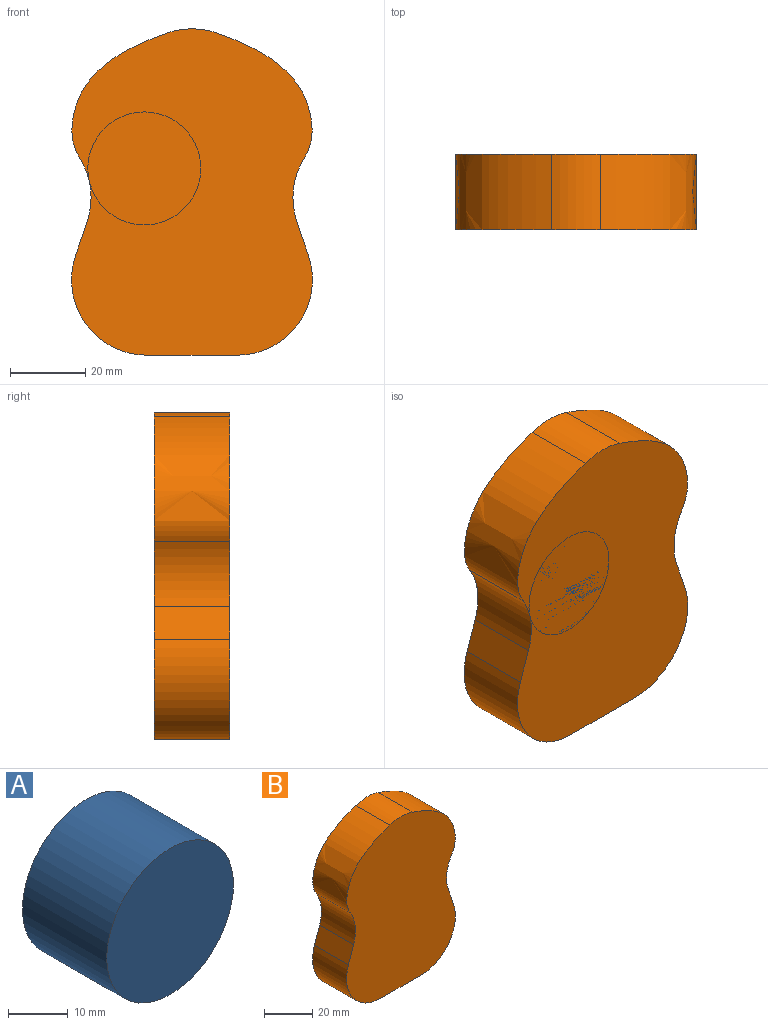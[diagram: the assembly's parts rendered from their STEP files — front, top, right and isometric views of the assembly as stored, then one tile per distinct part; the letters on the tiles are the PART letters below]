
ASSEMBLY  parts=2 mates=1
PART A: 3 faces, bbox 30x20x30 mm
  f0: cylinder r=15mm len=30mm, axis (0,-1,0), area 1885mm2, adj f1,f2
  f1: plane 30x30mm, normal (0,1,0), area 706.9mm2, adj f0
  f2: plane 30x30mm, normal (0,-1,0), area 706.9mm2, adj f0
PART B: 12 faces, bbox 65.7x20x86.6 mm
  f0: plane 23.92x20mm, normal (0,0,-1), area 478.4mm2, adj f5,f6,f7,f11
  f1: plane 20x8.75mm, normal (0.95,0,0.33), area 185.1mm2, adj f5,f6,f7,f8
  f2: extruded ~33.01x25.36mm, area 928mm2, adj f5,f6,f8,f9
  f3: extruded ~33.01x25.36mm, area 928mm2, adj f5,f6,f9,f10
  f4: plane 20x8.75mm, normal (-0.95,0,0.33), area 185.1mm2, adj f5,f6,f10,f11
  f5: plane 86.57x65.71mm, normal (0,-1,0), area 4720.8mm2, adj f0,f1,f2,f3,f4,f7,f8,f9
  f6: plane 86.57x65.71mm, normal (0,1,0), area 4720.8mm2, adj f0,f1,f2,f3,f4,f7,f8,f9
  f7: cylinder r=20mm len=26.51mm, axis (0,1,0), area 761mm2, adj f0,f1,f5,f6
  f8: cylinder r=20mm len=20mm, axis (0,1,0), area 358.4mm2, adj f1,f2,f5,f6
  f9: cylinder r=20mm len=20mm, axis (0,1,0), area 264.5mm2, adj f2,f3,f5,f6
  f10: cylinder r=20mm len=20mm, axis (0,1,0), area 358.4mm2, adj f3,f4,f5,f6
  f11: cylinder r=20mm len=26.51mm, axis (0,-1,0), area 761mm2, adj f0,f4,f5,f6
PLACE A rot(axis=(0,1,0),9.1deg) t=(-10.66,-8.22,6.74)mm
PLACE B t=(1.97,11.78,4.54)mm fixed
MATE planar A.f0 <-> B.f5  axis (0,-1,0) through (-10.66,-8.22,6.74)mm
